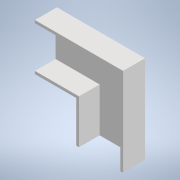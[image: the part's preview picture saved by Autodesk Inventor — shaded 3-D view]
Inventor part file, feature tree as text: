
AUTODESK INVENTOR PART (.ipt)
format: ipt  version: 2022 (Build 260153000, 153)  size: 147,456 bytes
history: native  units: mm
features: extrude x2, sketch x2, other x1, projected_geometry x1
ambient origin geometry x8: Origin, YZ Plane, XZ Plane, XY Plane, X Axis, Y Axis, Z Axis, Center Point
bodies: Body1 (feature_tree)
feature tree (6):
  other  "Твердое тело1"
  extrude  "Выдавливание1"  Depth=300.0mm
  extrude  "Выдавливание2"  Depth=300.0mm
  sketch  "Эскиз1"
  sketch  "Эскиз2"
  projected_geometry  "Спроецированная петля1"
